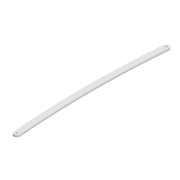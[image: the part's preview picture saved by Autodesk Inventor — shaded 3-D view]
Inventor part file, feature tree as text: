
AUTODESK INVENTOR PART (.ipt)
format: ipt  version: 2022 (Build 260153000, 153)  size: 93,696 bytes
history: native  units: mm
features: extrude x1, sketch x1
ambient origin geometry x8: Origin, YZ Plane, XZ Plane, XY Plane, X Axis, Y Axis, Z Axis, Center Point
bodies: Solid1 (feature_tree)
feature tree (2):
  extrude  "Extrusion1"  Depth=1500.0mm
  sketch  "Sketch1"  dims[d0=3.3mm d1=3.3mm d2=10.0mm d3=253.429mm d6=3.0mm d7=0.0mm d16=1500.0mm d17=1500.0mm]
